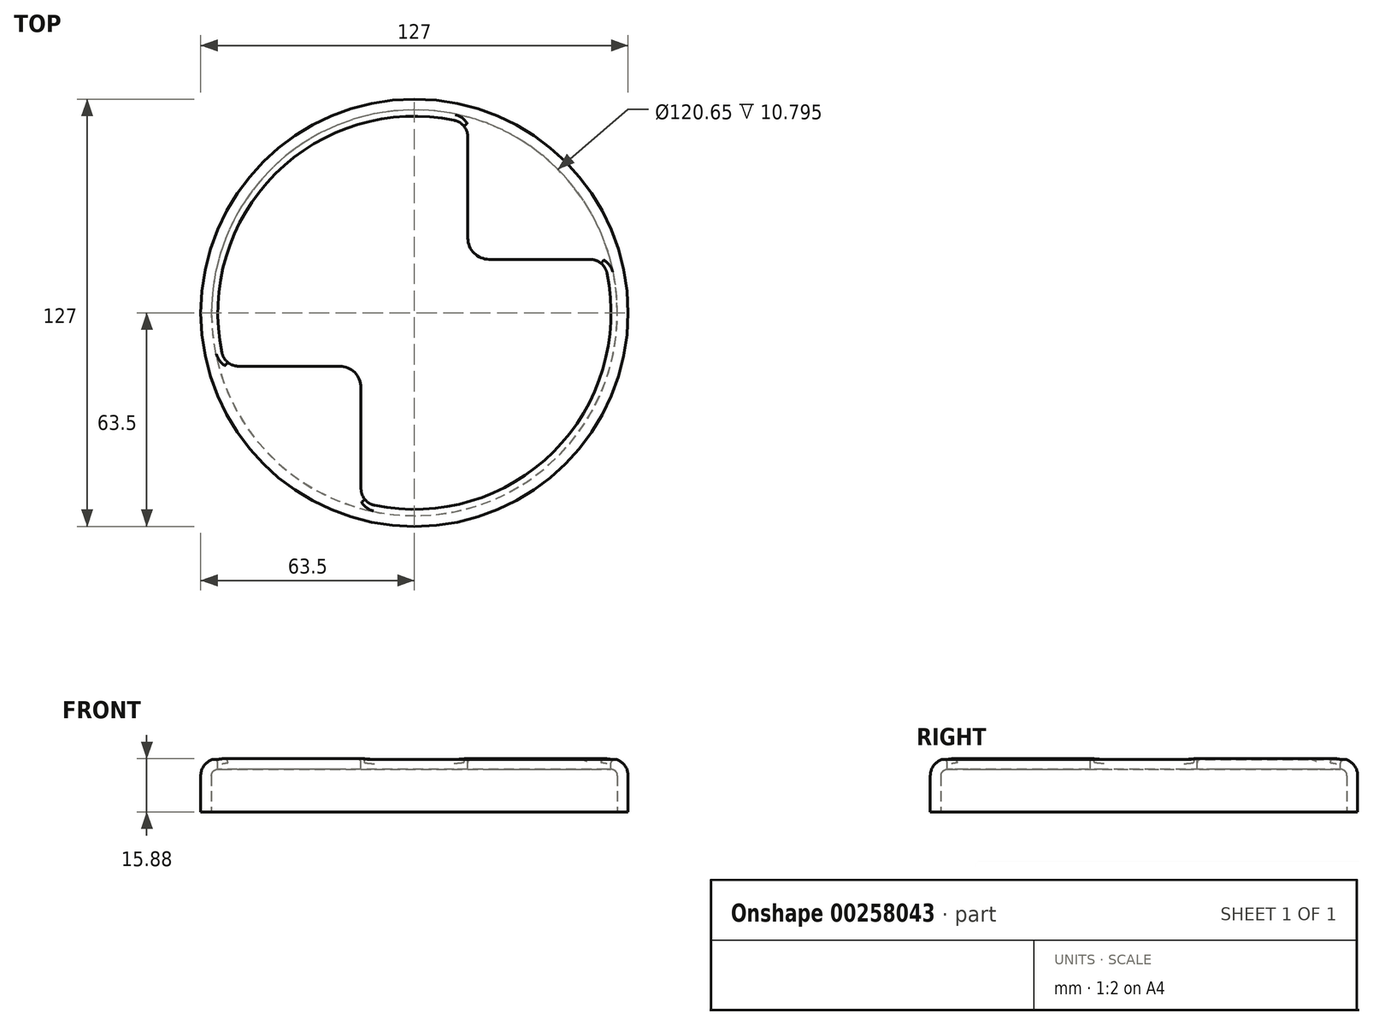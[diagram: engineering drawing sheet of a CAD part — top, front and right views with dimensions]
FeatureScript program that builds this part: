
annotation { "Feature Type Name" : "Feature", "Feature Type Description" : "" }
export const myFeature = defineFeature(function(context is Context, id is Id, definition is map)
    precondition{}
    {
        {
            var Q0;
            Q0=qCreatedBy(makeId("Top.planeOp"),FACE);
            var sketch = newSketch(context, id + "F0", { "sketchPlane" : qUnion([Q0])});
            skCircle(sketch, "E0", {"center": v(0, 0) * mm, "radius": 63.5 * mm});
            skSolve(sketch);
        }
        {
            var Q0;
            Q0 = qSketchRegion(id + "F0", true);
            extrude(context, id + "F1", {"entities" : qUnion([Q0]), "depth" : 15.88 * mm});
        }
        {
            var Q0;
            Q0=makeQuery(id+"F1.opExtrude","CAP_EDGE",EDGE,{"disambiguationData":[OSD([sQuery(id+"F0.wireOp",EDGE,"E0")])],"isStart":false});
            fillet(context, id + "F2", {"entities" : qUnion([Q0]), "radius" : 5.08 * mm, "tangentPropagation" : true, "allowEdgeOverflow" : false});
        }
        {
            var Q0;
            Q0=makeQuery(id+"F1.opExtrude","CAP_FACE",FACE,{"disambiguationData":[OSD([sQuery(id+"F0.wireOp",EDGE,"E0")])],"isStart":true});
            shell(context, id + "F3", {"entities" : qUnion([Q0]), "thickness" : 3.17 * mm});
        }
        {
            var Q0;
            Q0=makeQuery(id+"F1.opExtrude","CAP_FACE",FACE,{"disambiguationData":[OSD([sQuery(id+"F0.wireOp",EDGE,"E0")])],"isStart":false});
            var sketch = newSketch(context, id + "F4", { "sketchPlane" : qUnion([Q0])});
            skLineSegment(sketch, "E1.bottom", {"start": v(-15.88, 66.68) * mm, "end": v(-66.68, 66.68) * mm});
            skLineSegment(sketch, "E1.top", {"start": v(-22.23, 15.88) * mm, "end": v(-66.68, 15.87) * mm});
            skLineSegment(sketch, "E1.left", {"start": v(-15.88, 66.68) * mm, "end": v(-15.88, 22.23) * mm});
            skLineSegment(sketch, "E1.right", {"start": v(-66.68, 66.68) * mm, "end": v(-66.68, 15.88) * mm});
            skPoint(sketch, "E2.visualSharp", {"position": v(-15.88, 15.88) * mm});
            skArc(sketch, "E2.filletArc", {"start": v(-22.23, 15.88) * mm, "mid": v(-17.73, 17.73) * mm, "end": v(-15.88, 22.23) * mm});
            skArc(sketch, "E3.MirrorCS", {"start": v(22.23, 15.88) * mm, "mid": v(17.73, 17.73) * mm, "end": v(15.88, 22.23) * mm});
            skPoint(sketch, "E4.MirrorP", {"position": v(15.88, 15.88) * mm});
            skLineSegment(sketch, "E5.MirrorCS", {"start": v(15.88, 66.68) * mm, "end": v(66.68, 66.68) * mm});
            skLineSegment(sketch, "E6.MirrorCS", {"start": v(22.23, 15.88) * mm, "end": v(66.68, 15.87) * mm});
            skLineSegment(sketch, "E7.MirrorCS", {"start": v(66.68, 66.68) * mm, "end": v(66.68, 15.88) * mm});
            skLineSegment(sketch, "E8.MirrorCS", {"start": v(15.88, 66.68) * mm, "end": v(15.88, 22.23) * mm});
            skArc(sketch, "E9.MirrorCS", {"start": v(-22.23, -15.88) * mm, "mid": v(-17.73, -17.73) * mm, "end": v(-15.88, -22.23) * mm});
            skArc(sketch, "E10.MirrorCS", {"start": v(22.23, -15.88) * mm, "mid": v(17.73, -17.73) * mm, "end": v(15.88, -22.23) * mm});
            skLineSegment(sketch, "E11.MirrorCS", {"start": v(-22.23, -15.88) * mm, "end": v(-66.68, -15.87) * mm});
            skLineSegment(sketch, "E12.MirrorCS", {"start": v(-15.88, -66.68) * mm, "end": v(-15.88, -22.23) * mm});
            skPoint(sketch, "E13.MirrorP", {"position": v(-15.88, -15.88) * mm});
            skLineSegment(sketch, "E14.MirrorCS", {"start": v(66.68, -66.68) * mm, "end": v(66.68, -15.88) * mm});
            skLineSegment(sketch, "E15.MirrorCS", {"start": v(22.23, -15.88) * mm, "end": v(66.68, -15.87) * mm});
            skLineSegment(sketch, "E16.MirrorCS", {"start": v(-66.68, -66.68) * mm, "end": v(-66.68, -15.88) * mm});
            skPoint(sketch, "E17.MirrorP", {"position": v(15.88, -15.88) * mm});
            skLineSegment(sketch, "E18.MirrorCS", {"start": v(15.88, -66.68) * mm, "end": v(15.88, -22.23) * mm});
            skLineSegment(sketch, "E19.MirrorCS", {"start": v(-15.88, -66.68) * mm, "end": v(-66.68, -66.68) * mm});
            skLineSegment(sketch, "E20.MirrorCS", {"start": v(15.88, -66.68) * mm, "end": v(66.68, -66.68) * mm});
            skSolve(sketch);
        }
        {
            var Q0;
            {var subQ0=sQuery(id+"F4.wireOp",EDGE,"E2.filletArc");Q0=makeQuery(id+"F4.imprint","IMPRINT",FACE,{"disambiguationData":[TD([[makeQuery(id+"F4.imprint","IMPRINT",EDGE,{"derivedFrom":subQ0}),1.0]])]});}
            var Q1;
            {var subQ0=sQuery(id+"F4.wireOp",EDGE,"E3.MirrorCS");Q1=makeQuery(id+"F4.imprint","IMPRINT",FACE,{"disambiguationData":[TD([[makeQuery(id+"F4.imprint","IMPRINT",EDGE,{"derivedFrom":subQ0}),-1.0]])]});}
            var Q2;
            {var subQ0=sQuery(id+"F4.wireOp",EDGE,"E10.MirrorCS");Q2=makeQuery(id+"F4.imprint","IMPRINT",FACE,{"disambiguationData":[TD([[makeQuery(id+"F4.imprint","IMPRINT",EDGE,{"derivedFrom":subQ0}),1.0]])]});}
            var Q3;
            {var subQ0=sQuery(id+"F4.wireOp",EDGE,"E9.MirrorCS");Q3=makeQuery(id+"F4.imprint","IMPRINT",FACE,{"disambiguationData":[TD([[makeQuery(id+"F4.imprint","IMPRINT",EDGE,{"derivedFrom":subQ0}),-1.0]])]});}
            extrude(context, id + "F5", {"entities" : qUnion([Q0, Q1, Q2, Q3]), "operationType" : NewBodyOperationType.REMOVE, "oppositeDirection" : true, "depth" : 25.4 * mm});
        }
        {
            var Q0;
            Q0=makeQuery(id+"F5.boolean.opBoolean","COPY",EDGE,{"derivedFrom":makeQuery(id+"F5.opExtrude","SWEPT_EDGE",EDGE,{"disambiguationData":[OSD([sQuery(id+"F0.wireOp",EDGE,"E0"),sQuery(id+"F4.wireOp",EDGE,"E12.MirrorCS")])]})});
            var Q1;
            Q1=makeQuery(id+"F5.boolean.opBoolean","COPY",EDGE,{"derivedFrom":makeQuery(id+"F5.opExtrude","SWEPT_EDGE",EDGE,{"disambiguationData":[OSD([sQuery(id+"F0.wireOp",EDGE,"E0"),sQuery(id+"F4.wireOp",EDGE,"E18.MirrorCS")])]})});
            var Q2;
            Q2=makeQuery(id+"F5.boolean.opBoolean","COPY",EDGE,{"derivedFrom":makeQuery(id+"F5.opExtrude","SWEPT_EDGE",EDGE,{"disambiguationData":[OSD([sQuery(id+"F0.wireOp",EDGE,"E0"),sQuery(id+"F4.wireOp",EDGE,"E15.MirrorCS")])]})});
            var Q3;
            Q3=makeQuery(id+"F5.boolean.opBoolean","COPY",EDGE,{"derivedFrom":makeQuery(id+"F5.opExtrude","SWEPT_EDGE",EDGE,{"disambiguationData":[OSD([sQuery(id+"F0.wireOp",EDGE,"E0"),sQuery(id+"F4.wireOp",EDGE,"E6.MirrorCS")])]})});
            var Q4;
            Q4=makeQuery(id+"F5.boolean.opBoolean","COPY",EDGE,{"derivedFrom":makeQuery(id+"F5.opExtrude","SWEPT_EDGE",EDGE,{"disambiguationData":[OSD([sQuery(id+"F0.wireOp",EDGE,"E0"),sQuery(id+"F4.wireOp",EDGE,"E8.MirrorCS")])]})});
            var Q5;
            Q5=makeQuery(id+"F5.boolean.opBoolean","COPY",EDGE,{"derivedFrom":makeQuery(id+"F5.opExtrude","SWEPT_EDGE",EDGE,{"disambiguationData":[OSD([sQuery(id+"F0.wireOp",EDGE,"E0"),sQuery(id+"F4.wireOp",EDGE,"E1.left")])]})});
            var Q6;
            Q6=makeQuery(id+"F5.boolean.opBoolean","COPY",EDGE,{"derivedFrom":makeQuery(id+"F5.opExtrude","SWEPT_EDGE",EDGE,{"disambiguationData":[OSD([sQuery(id+"F0.wireOp",EDGE,"E0"),sQuery(id+"F4.wireOp",EDGE,"E1.top")])]})});
            var Q7;
            Q7=makeQuery(id+"F5.boolean.opBoolean","COPY",EDGE,{"derivedFrom":makeQuery(id+"F5.opExtrude","SWEPT_EDGE",EDGE,{"disambiguationData":[OSD([sQuery(id+"F0.wireOp",EDGE,"E0"),sQuery(id+"F4.wireOp",EDGE,"E11.MirrorCS")])]})});
            fillet(context, id + "F6", {"entities" : qUnion([Q0, Q1, Q2, Q3, Q4, Q5, Q6, Q7]), "radius" : 5.08 * mm, "tangentPropagation" : true, "allowEdgeOverflow" : false});
        }
        {
            var Q0;
            Q0=makeQuery(id+"F5.boolean.opBoolean","COPY",EDGE,{"derivedFrom":makeQuery(id+"F5.opExtrude","CAP_EDGE",EDGE,{"disambiguationData":[OSD([sQuery(id+"F4.wireOp",EDGE,"E1.top")])],"isStart":true})});
            var Q1;
            Q1=makeQuery(id+"F5.boolean.opBoolean","COPY",EDGE,{"derivedFrom":makeQuery(id+"F5.opExtrude","CAP_EDGE",EDGE,{"disambiguationData":[OSD([sQuery(id+"F4.wireOp",EDGE,"E11.MirrorCS")])],"isStart":true})});
            var Q2;
            Q2=makeQuery(id+"F5.boolean.opBoolean","COPY",EDGE,{"derivedFrom":makeQuery(id+"F5.opExtrude","CAP_EDGE",EDGE,{"disambiguationData":[OSD([sQuery(id+"F4.wireOp",EDGE,"E6.MirrorCS")])],"isStart":true})});
            var Q3;
            Q3=makeQuery(id+"F5.boolean.opBoolean","COPY",EDGE,{"derivedFrom":makeQuery(id+"F5.opExtrude","CAP_EDGE",EDGE,{"disambiguationData":[OSD([sQuery(id+"F4.wireOp",EDGE,"E15.MirrorCS")])],"isStart":true})});
            fillet(context, id + "F7", {"entities" : qUnion([Q0, Q1, Q2, Q3]), "radius" : 1.27 * mm, "tangentPropagation" : true, "allowEdgeOverflow" : false});
        }
    });
